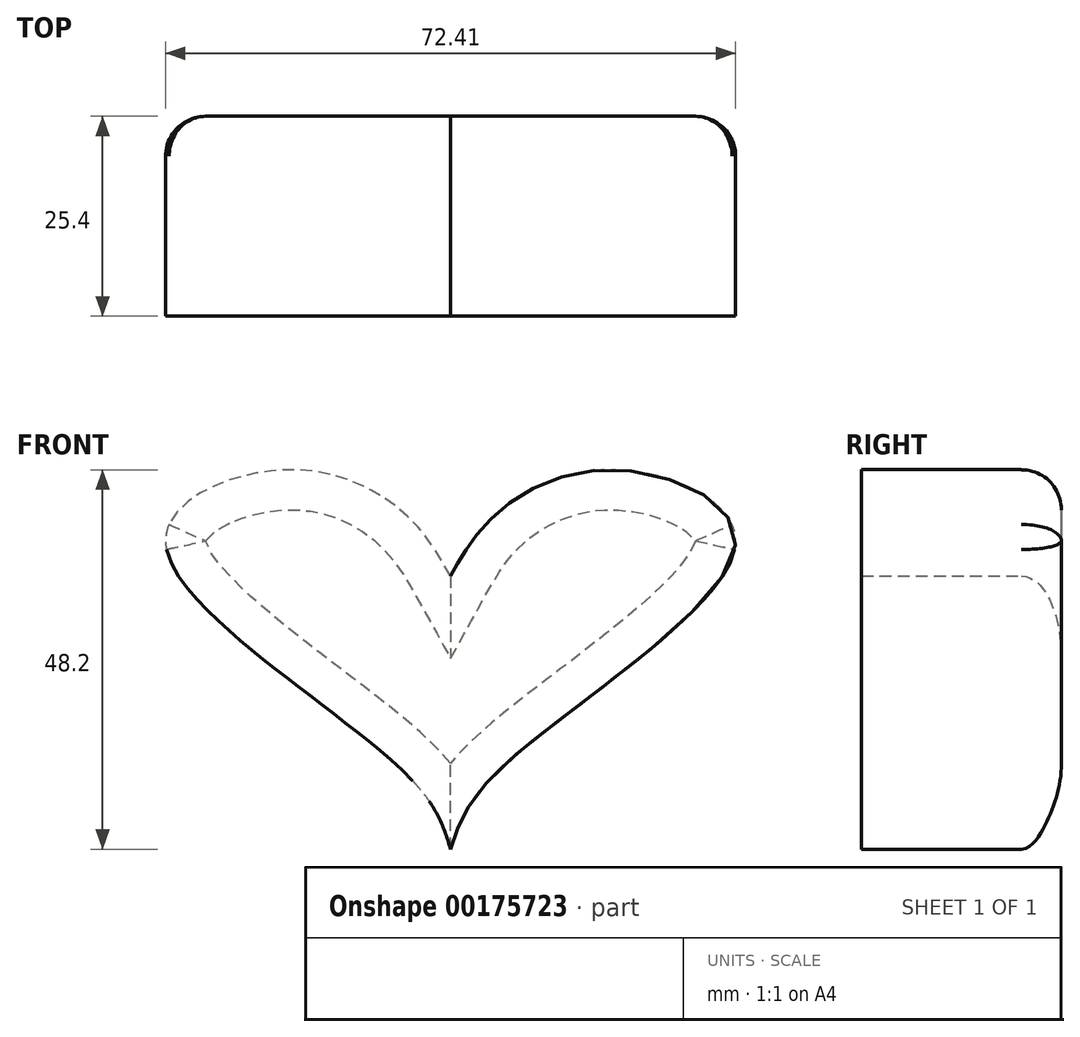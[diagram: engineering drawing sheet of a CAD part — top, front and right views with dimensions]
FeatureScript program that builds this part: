
annotation { "Feature Type Name" : "Feature", "Feature Type Description" : "" }
export const myFeature = defineFeature(function(context is Context, id is Id, definition is map)
    precondition{}
    {
        {
            var Q0;
            Q0=qCreatedBy(makeId("Front.planeOp"),FACE);
            var sketch = newSketch(context, id + "F0", { "sketchPlane" : qUnion([Q0])});
            skLineSegment(sketch, "E0", {"start": v(-72.61, 41.35) * mm, "end": v(-72.61, 6.64) * mm});
            skFitSpline(sketch, "E1", {"points": [v(-72.61, 41.35) * mm, v(-70.67, 44.64) * mm, v(-65.88, 50.02) * mm, v(-51.07, 54.8) * mm, v(-36.41, 45.53) * mm, v(-66.18, 16.96) * mm, v(-72.61, 6.64) * mm], "startDerivative": vector(20.22, 36.43) * mm, "endDerivative": vector(-18.05, -58.53) * mm});
            skFitSpline(sketch, "E2.MirrorCS", {"points": [v(-72.61, 41.35) * mm, v(-74.56, 44.64) * mm, v(-79.34, 50.02) * mm, v(-94.15, 54.8) * mm, v(-108.81, 45.53) * mm, v(-79.04, 16.96) * mm, v(-72.61, 6.64) * mm], "startDerivative": vector(-20.22, 36.43) * mm, "endDerivative": vector(18.05, -58.53) * mm});
            skSolve(sketch);
        }
        {
            var Q0;
            Q0=qSketchRegion(id+"F0",true);
            extrude(context, id + "F1", {"entities" : qUnion([Q0]), "endBound" : BoundingType.SYMMETRIC, "depth" : 25.4 * mm});
        }
        {
            var Q0;
            Q0=makeQuery(id+"F1.opExtrude","CAP_FACE",FACE,{"disambiguationData":[OSD([sQuery(id+"F0.wireOp",EDGE,"E1"),sQuery(id+"F0.wireOp",EDGE,"E2.MirrorCS")])],"isStart":true});
            fillet(context, id + "F2", {"entities" : qUnion([Q0]), "radius" : 5.08 * mm, "tangentPropagation" : true, "allowEdgeOverflow" : false});
        }
    });
